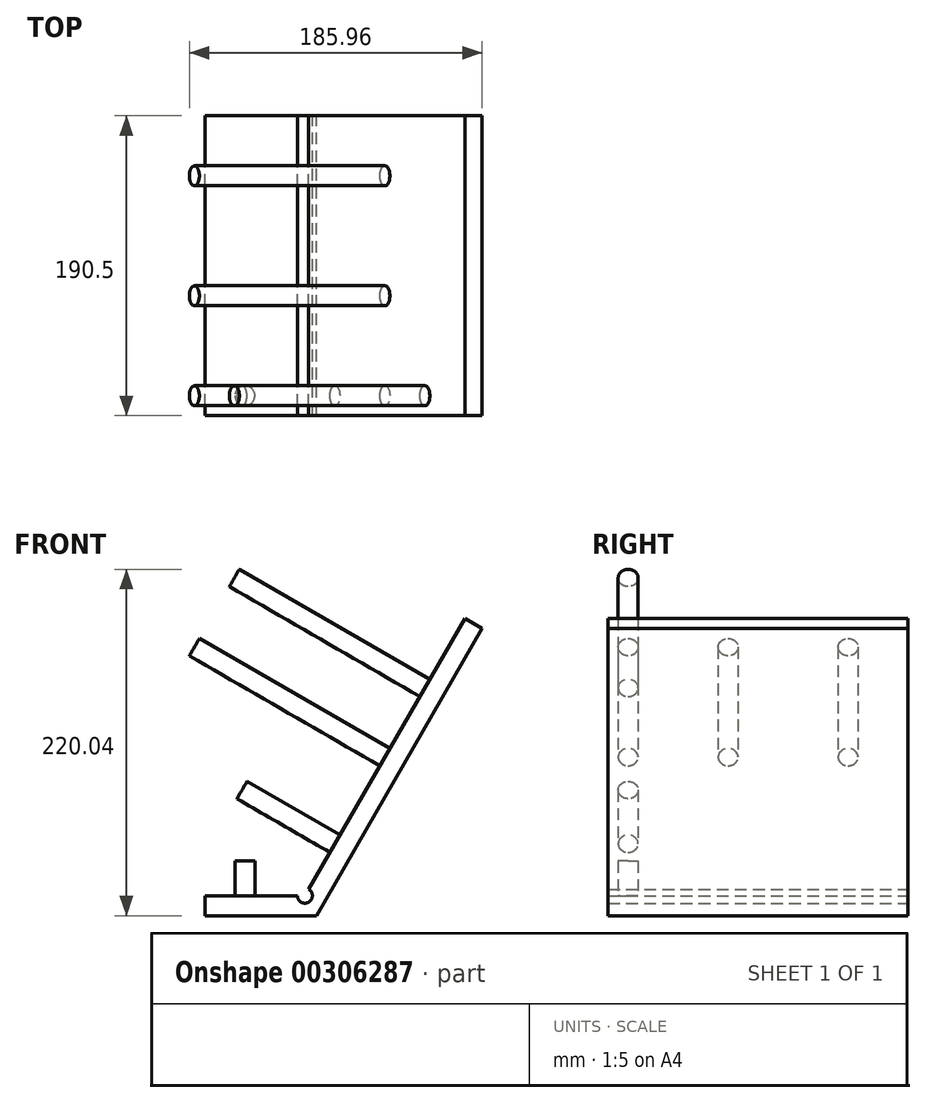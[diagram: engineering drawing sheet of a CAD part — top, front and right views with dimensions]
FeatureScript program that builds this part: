
annotation { "Feature Type Name" : "Feature", "Feature Type Description" : "" }
export const myFeature = defineFeature(function(context is Context, id is Id, definition is map)
    precondition{}
    {
        {
            var Q0;
            Q0=qCreatedBy(makeId("Front.planeOp"),FACE);
            var sketch = newSketch(context, id + "F0", { "sketchPlane" : qUnion([Q0])});
            skLineSegment(sketch, "E0", {"start": v(0, 0) * mm, "end": v(0, -12.7) * mm});
            skLineSegment(sketch, "E1", {"start": v(0, -12.7) * mm, "end": v(70.84, -12.7) * mm});
            skLineSegment(sketch, "E2", {"start": v(70.84, -12.7) * mm, "end": v(176.11, 169.63) * mm});
            skLineSegment(sketch, "E3", {"start": v(176.11, 169.63) * mm, "end": v(165.11, 175.98) * mm});
            skLineSegment(sketch, "E4", {"start": v(165.11, 175.98) * mm, "end": v(65.89, 4.12) * mm});
            skLineSegment(sketch, "E5", {"start": v(58.75, 0) * mm, "end": v(0, 0) * mm});
            skArc(sketch, "E6", {"start": v(58.75, 0) * mm, "mid": v(65.89, -4.12) * mm, "end": v(65.89, 4.12) * mm});
            skSolve(sketch);
        }
        {
            var Q0;
            Q0 = qSketchRegion(id + "F0", true);
            extrude(context, id + "F1", {"entities" : qUnion([Q0]), "depth" : 190.5 * mm});
        }
        {
            var Q0;
            Q0=makeQuery(id+"F1.opExtrude","SWEPT_FACE",FACE,{"disambiguationData":[OSD([sQuery(id+"F0.wireOp",EDGE,"E5")])]});
            var sketch = newSketch(context, id + "F2", { "sketchPlane" : qUnion([Q0])});
            skPoint(sketch, "E7", {"position": v(25.4, -177.8) * mm});
            skCircle(sketch, "E8", {"center": v(25.4, -177.8) * mm, "radius": 6.35 * mm});
            skSolve(sketch);
        }
        {
            var Q0;
            Q0=makeQuery(id+"F1.opExtrude","SWEPT_FACE",FACE,{"disambiguationData":[OSD([sQuery(id+"F0.wireOp",EDGE,"E4")])]});
            var sketch = newSketch(context, id + "F3", { "sketchPlane" : qUnion([Q0])});
            skPoint(sketch, "E9", {"position": v(177.8, 69.86) * mm});
            skPoint(sketch, "E10", {"position": v(177.8, 133.36) * mm});
            skPoint(sketch, "E11", {"position": v(177.8, 184.16) * mm});
            skPoint(sketch, "E12", {"position": v(114.3, 133.36) * mm});
            skPoint(sketch, "E13", {"position": v(38.1, 133.36) * mm});
            skCircle(sketch, "E14", {"center": v(177.8, 69.86) * mm, "radius": 6.35 * mm});
            skCircle(sketch, "E15", {"center": v(177.8, 133.36) * mm, "radius": 6.35 * mm});
            skCircle(sketch, "E16", {"center": v(177.8, 184.16) * mm, "radius": 6.35 * mm});
            skCircle(sketch, "E17", {"center": v(114.3, 133.36) * mm, "radius": 6.35 * mm});
            skCircle(sketch, "E18", {"center": v(38.1, 133.36) * mm, "radius": 6.35 * mm});
            skSolve(sketch);
        }
        {
            var Q0;
            Q0 = qSketchRegion(id + "F2", true);
            extrude(context, id + "F4", {"entities" : qUnion([Q0]), "operationType" : NewBodyOperationType.ADD, "depth" : 22 * mm});
        }
        {
            var Q0;
            Q0=makeQuery(id+"F3.imprint","IMPRINT",FACE,{"disambiguationData":[TD([[makeQuery(id+"F3.imprint","IMPRINT",EDGE,{"derivedFrom":sQuery(id+"F3.wireOp",EDGE,"E14")}),1.0]])]});
            extrude(context, id + "F5", {"entities" : qUnion([Q0]), "operationType" : NewBodyOperationType.ADD, "depth" : 68.15 * mm});
        }
        {
            var Q0;
            Q0=makeQuery(id+"F3.imprint","IMPRINT",FACE,{"disambiguationData":[TD([[makeQuery(id+"F3.imprint","IMPRINT",EDGE,{"derivedFrom":sQuery(id+"F3.wireOp",EDGE,"E15")}),1.0]])]});
            var Q1;
            Q1=makeQuery(id+"F3.imprint","IMPRINT",FACE,{"disambiguationData":[TD([[makeQuery(id+"F3.imprint","IMPRINT",EDGE,{"derivedFrom":sQuery(id+"F3.wireOp",EDGE,"E17")}),1.0]])]});
            var Q2;
            Q2=makeQuery(id+"F3.imprint","IMPRINT",FACE,{"disambiguationData":[TD([[makeQuery(id+"F3.imprint","IMPRINT",EDGE,{"derivedFrom":sQuery(id+"F3.wireOp",EDGE,"E18")}),1.0]])]});
            var Q3;
            Q3=makeQuery(id+"F3.imprint","IMPRINT",FACE,{"disambiguationData":[TD([[makeQuery(id+"F3.imprint","IMPRINT",EDGE,{"derivedFrom":sQuery(id+"F3.wireOp",EDGE,"E16")}),1.0]])]});
            extrude(context, id + "F6", {"entities" : qUnion([Q0, Q1, Q2, Q3]), "operationType" : NewBodyOperationType.ADD, "depth" : 139.7 * mm});
        }
    });
